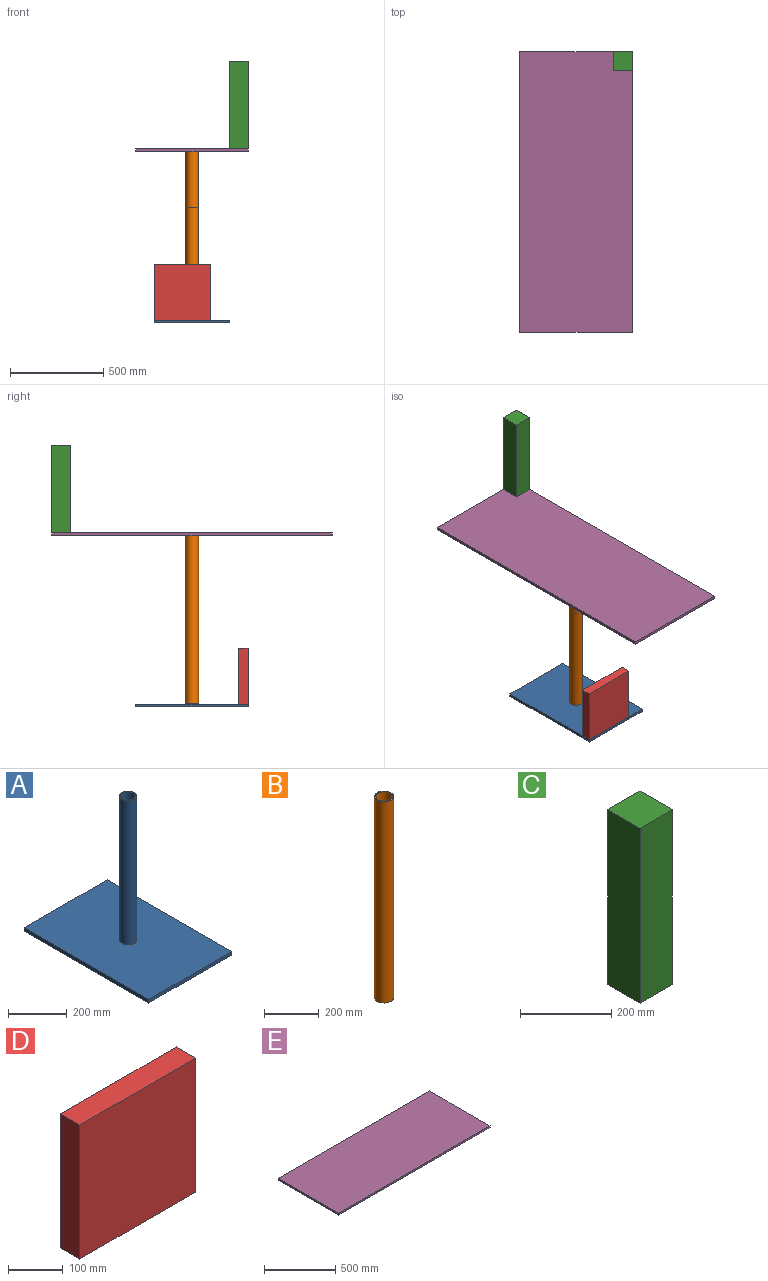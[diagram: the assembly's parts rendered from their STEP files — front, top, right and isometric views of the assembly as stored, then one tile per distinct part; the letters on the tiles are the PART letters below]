
ASSEMBLY  parts=5 mates=5
PART A: 10 faces, bbox 400x600x615 mm
  f0: cylinder r=25mm len=600mm, axis (0,0,-1), area 94247.8mm2, adj f2,f9
  f1: cylinder r=30mm len=600mm, axis (0,0,-1), area 113097.3mm2, adj f2,f3
  f2: plane 60x60mm, normal (0,0,1), area 863.9mm2, adj f0,f1
  f3: plane 600x400mm, normal (0,0,1), area 237172.6mm2, adj f1,f5,f6,f7,f8
  f4: plane 600x400mm, normal (0,0,-1), area 240000mm2, adj f5,f6,f7,f8
  f5: plane 600x15mm, normal (-1,0,0), area 9000mm2, adj f3,f4,f6,f8
  f6: plane 400x15mm, normal (0,-1,0), area 6000mm2, adj f3,f4,f5,f7
  f7: plane 600x15mm, normal (1,0,0), area 9000mm2, adj f3,f4,f6,f8
  f8: plane 400x15mm, normal (0,1,0), area 6000mm2, adj f3,f4,f5,f7
  f9: plane 50x50mm, normal (0,0,1), area 1963.5mm2, adj f0
PART B: 4 faces, bbox 70x70x900 mm
  f0: cylinder r=30mm len=900mm, axis (0,0,-1), area 169646mm2, adj f2,f3
  f1: cylinder r=35mm len=900mm, axis (0,0,-1), area 197920.3mm2, adj f2,f3
  f2: plane 70x70mm, normal (0,0,1), area 1021mm2, adj f0,f1
  f3: plane 70x70mm, normal (0,0,-1), area 1021mm2, adj f0,f1
PART C: 6 faces, bbox 100x100x470 mm
  f0: plane 470x100mm, normal (-1,0,0), area 47000mm2, adj f1,f3,f4,f5
  f1: plane 470x100mm, normal (0,-1,0), area 47000mm2, adj f0,f2,f4,f5
  f2: plane 470x100mm, normal (1,0,0), area 47000mm2, adj f1,f3,f4,f5
  f3: plane 470x100mm, normal (0,1,0), area 47000mm2, adj f0,f2,f4,f5
  f4: plane 100x100mm, normal (0,0,1), area 10000mm2, adj f0,f1,f2,f3
  f5: plane 100x100mm, normal (0,0,-1), area 10000mm2, adj f0,f1,f2,f3
PART D: 6 faces, bbox 300x50x300 mm
  f0: plane 300x50mm, normal (-1,0,0), area 15000mm2, adj f1,f3,f4,f5
  f1: plane 300x300mm, normal (0,-1,0), area 90000mm2, adj f0,f2,f4,f5
  f2: plane 300x50mm, normal (1,0,0), area 15000mm2, adj f1,f3,f4,f5
  f3: plane 300x300mm, normal (0,1,0), area 90000mm2, adj f0,f2,f4,f5
  f4: plane 300x50mm, normal (0,0,1), area 15000mm2, adj f0,f1,f2,f3
  f5: plane 300x50mm, normal (0,0,-1), area 15000mm2, adj f0,f1,f2,f3
PART E: 6 faces, bbox 1500x600x15 mm
  f0: plane 1500x15mm, normal (0,1,0), area 22500mm2, adj f1,f3,f4,f5
  f1: plane 600x15mm, normal (-1,0,0), area 9000mm2, adj f0,f2,f4,f5
  f2: plane 1500x15mm, normal (0,-1,0), area 22500mm2, adj f1,f3,f4,f5
  f3: plane 600x15mm, normal (1,0,0), area 9000mm2, adj f0,f2,f4,f5
  f4: plane 1500x600mm, normal (0,0,1), area 900000mm2, adj f0,f1,f2,f3
  f5: plane 1500x600mm, normal (0,0,-1), area 900000mm2, adj f0,f1,f2,f3
PLACE A t=(-200,-300,15)mm
PLACE B rot(axis=(0,0,-1),90deg) t=(-200,-300,15.54)mm
PLACE C t=(0,350,930.54)mm
PLACE D t=(-407.11,-600,15)mm
PLACE E rot(axis=(0,0,-1),90deg) t=(-200,-300,15.54)mm
MATE fastened E.f4 <-> C.f5  axis (0,0,1) through (100,450,930.54)mm
MATE fastened E.f5 <-> B.f1  axis (0,0,-1) through (-200,-300,915.54)mm
MATE parallel E.f2 <-> A.f5  axis (-1,0,0) through (-500,-300,923.04)mm
MATE fastened D.f1 <-> A.f6  axis (0,-1,0) through (-400,-600,15)mm
MATE cylindrical A.f1 <-> B.f1  axis (0,0,-1) through (-200,-300,615)mm
